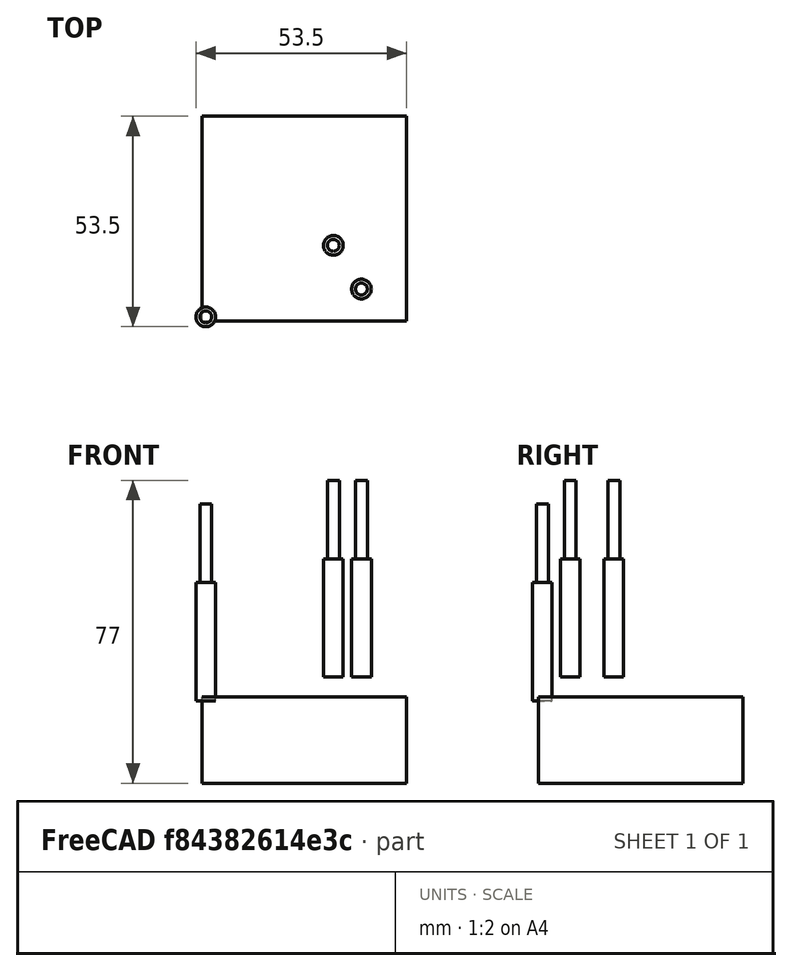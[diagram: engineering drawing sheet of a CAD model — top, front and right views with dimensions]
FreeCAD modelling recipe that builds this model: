
FCSTD DOCUMENT  (FreeCAD 1.0R39109 (Git))
Label: test CNCFCStd
License: All rights reserved
LicenseURL: http://en.wikipedia.org/wiki/All_rights_reserved
objects: Part::FeaturePython×6, Path::FeaturePython×4, Mesh::FeaturePython×4, Sketcher::SketchObject×3, App::DocumentObjectGroup×3, PartDesign::Pocket×2, PartDesign::Pad×1, App::FeaturePython×1, PartDesign::Body×1
note: 23 computed .brp shape members not serialized (recipe doc carries the construction recipe); baked Part::Feature solids carry a one-line shape summary decoded from their .brp

FEATURE [Sketcher::SketchObject] Sketch
  ArcFitTolerance = 1e-06
  AttachmentSupport = -> [XY_Plane]
  FullyConstrained = false
  MakeInternals = false
  MapMode = 5
  sketch-geometry (5):
    g0: LineSegment StartX=-25 StartY=25 StartZ=0 EndX=-25 EndY=-25 EndZ=0
    g1: LineSegment StartX=-25 StartY=-25 StartZ=0 EndX=25 EndY=-25 EndZ=0
    g2: LineSegment StartX=25 StartY=-25 StartZ=0 EndX=25 EndY=25 EndZ=0
    g3: LineSegment StartX=25 StartY=25 StartZ=0 EndX=-25 EndY=25 EndZ=0
    g4: Circle CenterX=-12.7394 CenterY=-12.191 CenterZ=0 NormalX=0 NormalY=0 NormalZ=1 AngleXU=0 Radius=4.56572
  constraints (11):
    c: Coincident(g0,g1)
    c: Coincident(g1,g2)
    c: Coincident(g2,g3)
    c: Coincident(g3,g0)
    c: Vertical(g0)
    c: Vertical(g2)
    c: Horizontal(g1)
    c: Horizontal(g3)
    c: Distance(g3,g3) = 50
    c: Distance(g0,g0) = 50
    c: Symmetric(g0,g1,g-1)
FEATURE [PartDesign::Pad] Pad
  Direction = (0,0,1)
  Length = 20
  Length2 = 0
  Profile = -> Sketch
  ReferenceAxis = -> Sketch [N_Axis]
  Reversed = true
  Suppressed = false
  Type = 0
FEATURE [Sketcher::SketchObject] Sketch001
  ArcFitTolerance = 1e-06
  AttachmentSupport = -> [XY_Plane]
  FullyConstrained = false
  MakeInternals = false
  MapMode = 5
  sketch-geometry (4):
    g0: LineSegment StartX=-18.6884 StartY=17.0009 StartZ=0 EndX=-18.6884 EndY=-0.101786 EndZ=0
    g1: LineSegment StartX=-18.6884 StartY=-0.101786 StartZ=0 EndX=17.0304 EndY=-0.101786 EndZ=0
    g2: LineSegment StartX=17.0304 StartY=-0.101786 StartZ=0 EndX=17.0304 EndY=17.0009 EndZ=0
    g3: LineSegment StartX=17.0304 StartY=17.0009 StartZ=0 EndX=-18.6884 EndY=17.0009 EndZ=0
  constraints (8):
    c: Coincident(g0,g1)
    c: Coincident(g1,g2)
    c: Coincident(g2,g3)
    c: Coincident(g3,g0)
    c: Vertical(g0)
    c: Vertical(g2)
    c: Horizontal(g1)
    c: Horizontal(g3)
FEATURE [PartDesign::Pocket] Pocket
  BaseFeature = -> Pad
  Direction = (0,0,-1)
  Length = 10
  Length2 = 5
  Profile = -> Sketch001
  ReferenceAxis = -> Sketch001 [N_Axis]
  Suppressed = false
  Type = 0
FEATURE [App::FeaturePython] SetupSheet  # Path/CAM operation (typed FeaturePython)
  ClearanceHeightExpression = OpStockZMax+SetupSheet.ClearanceHeightOffset
  ClearanceHeightOffset = 5
  CoolantMode = 0
  CoolantModes = None | Flood | Mist
  FinalDepthExpression = OpFinalDepth
  HorizRapid = 0
  SafeHeightExpression = OpStockZMax+SetupSheet.SafeHeightOffset
  SafeHeightOffset = 3
  StartDepthExpression = OpStartDepth
  StepDownExpression = OpToolDiameter
  VertRapid = 0
FEATURE [Part::FeaturePython] ToolBit  label="Endmill"  # Path/CAM toolbit (typed FeaturePython)
  BitPropertyNames = Chipload | CuttingEdgeHeight | Diameter | Flutes | Length | Material | ShankDiameter | SpindleDirection
  BitShape = <path>
  Chipload = 0
  CuttingEdgeHeight = 30
  Diameter = 5
  Flutes = 0
  Length = 50
  Material = 0
  ShankDiameter = 3
  ShapeName = endmill
  SpindleDirection = 0
FEATURE [Path::FeaturePython] TC__Default_Tool  label="TC: Default Tool"  # Path/CAM operation (typed FeaturePython)
  HorizFeed = 0
  HorizRapid = 0
  SpindleDir = 0
  SpindleSpeed = 0
  Tool = -> ToolBit
  ToolNumber = 1
  VertFeed = 0
  VertRapid = 0
  expr: HorizRapid = SetupSheet.HorizRapid
  expr: VertRapid = SetupSheet.VertRapid
FEATURE [Part::FeaturePython] ToolBit001  label="5mm Endmill"  # Path/CAM toolbit (typed FeaturePython)
  BitPropertyNames = Chipload | CuttingEdgeHeight | Diameter | Flutes | Length | Material | ShankDiameter | SpindleDirection
  BitShape = <path>
  Chipload = 0
  CuttingEdgeHeight = 30
  Diameter = 5
  File = <userpath>/AppData/Roaming/FreeCAD/Macro/Bit/5mm_Endmill.fctb
  Flutes = 0
  Length = 50
  Material = 0
  ShankDiameter = 3
  ShapeName = endmill
  SpindleDirection = 0
FEATURE [Path::FeaturePython] _mm_Endmill  label="5mm Endmill001"  # Path/CAM operation (typed FeaturePython)
  HorizFeed = 2
  HorizRapid = 0
  SpindleDir = 0
  SpindleSpeed = 5000
  Tool = -> ToolBit001
  ToolNumber = 2
  VertFeed = 2
  VertRapid = 0
  expr: HorizRapid = SetupSheet.HorizRapid
  expr: VertRapid = SetupSheet.VertRapid
FEATURE [App::DocumentObjectGroup] Tools
  Group = -> [TC__Default_Tool,_mm_Endmill]
FEATURE [Sketcher::SketchObject] Sketch002
  ArcFitTolerance = 1e-06
  AttachmentSupport = -> [XY_Plane]
  FullyConstrained = false
  MakeInternals = false
  MapMode = 5
  sketch-geometry (4):
    g0: ArcOfCircle CenterX=7.55026 CenterY=-9.04879 CenterZ=0 NormalX=0 NormalY=0 NormalZ=1 AngleXU=0 Radius=4.73311 StartAngle=0.866824 EndAngle=4.00842
    g1: ArcOfCircle CenterX=16.0485 CenterY=-16.2646 CenterZ=0 NormalX=0 NormalY=0 NormalZ=1 AngleXU=0 Radius=4.73311 StartAngle=4.00842 EndAngle=7.15001
    g2: LineSegment StartX=10.6138 StartY=-5.44084 StartZ=0 EndX=19.112 EndY=-12.6567 EndZ=0
    g3: LineSegment StartX=4.48675 StartY=-12.6567 StartZ=0 EndX=12.985 EndY=-19.8726 EndZ=0
  constraints (5):
    c: Tangent(g0,g2) = 1.5708
    c: Tangent(g0,g3) = -1.5708
    c: Tangent(g1,g2) = 1.5708
    c: Tangent(g1,g3) = -1.5708
    c: Equal(g0,g1)
FEATURE [PartDesign::Pocket] Pocket001
  BaseFeature = -> Pocket
  Direction = (0,0,-1)
  Length = 10
  Length2 = 5
  Profile = -> Sketch002
  ReferenceAxis = -> Sketch002 [N_Axis]
  Suppressed = false
  Type = 0
FEATURE [PartDesign::Body] Body
  AllowCompound = false
  Group = -> [Sketch,Pad,Sketch001,Pocket,Sketch002,Pocket001]
  Origin = -> Origin
  Tip = -> Pocket001
FEATURE [Part::FeaturePython] Clone  label="Model-Body"  # Draft clone (typed FeaturePython)
  AttacherType = Attacher::AttachEngine3D
  Fuse = false
  Objects = -> [Body]
  PathResource = Model
  Placement = pos=(25,25,0) rot=(0,0,1;0rad)
  Scale = (1,1,1)
FEATURE [App::DocumentObjectGroup] Model
  Group = -> [Clone]
FEATURE [Part::FeaturePython] Stock001  # WARN: FeaturePython — macro-defined, semantics opaque (R4)
  Base = -> Model
  ExtXneg = 1
  ExtXpos = 1
  ExtYneg = 1
  ExtYpos = 1
  ExtZneg = 1
  ExtZpos = 1
  Placement = pos=(0,0,-20) rot=(0,0,1;0rad)
  StockType = FromBase
FEATURE [Path::FeaturePython] Pocket_Shape  # Path/CAM operation (typed FeaturePython)
  Active = true
  AreaParams:
    Tolerance = 1e-07
    FitArcs = True
    Simplify = False
    CleanDistance = 0.0
    Accuracy = 0.01
    Unit = 1.0
    MinArcPoints = 4
    MaxArcPoints = 100
    ClipperScale = 10000000.0
    Fill = 0
    Coplanar = 0
    Reorient = True
    Outline = False
    Explode = False
    OpenMode = 0
    Deflection = 0.01
    SubjectFill = 0
    ClipFill = 0
    Offset = 0.0
    ExtraPass = 0
    Stepover = 0.0
    LastStepover = 0.0
    JoinType = 0
    EndType = 0
    MiterLimit = 2.0
    RoundPrecision = 0.0
    PocketMode = 2
    ToolRadius = 2.5
    PocketExtraOffset = 0.0
    PocketStepover = 5.0
    PocketLastStepover = 0.0
    FromCenter = True
    Angle = 45.0
    AngleShift = 0.0
    Shift = 0.0
    Thicken = False
    SectionCount = -1
    Stepdown = 1.0
    SectionOffset = 0.0
    SectionTolerance = 1e-06
    SectionMode = 2
    Project = False
  Base = -> [Clone]
  ClearanceHeight = 6
  CoolantMode = 0
  CutMode = 0
  CycleTime = 00:02:08
  ExtensionCorners = true
  ExtensionLengthDefault = 2.5
  ExtraOffset = 0
  FinalDepth = -10
  FinishDepth = 0
  KeepToolDown = false
  MinTravel = false
  OffsetPattern = 1
  OpFinalDepth = -10
  OpStartDepth = 1
  OpStockZMax = 1
  OpStockZMin = -21
  OpToolDiameter = 5
  PathParams = {'orientation': 1, 'feedrate': 2.0, 'feedrate_v': 2.0, 'verbose': True, 'resume_height': 4.0, 'retraction': 6.0, 'return_end': True, 'preamble': False, 'sort_mode': 0}
  PocketLastStepOver = 0
  SafeHeight = 4
  SplitArcs = false
  StartAt = 0
  StartDepth = 1
  StartPoint = (0,0,0)
  StepDown = 5
  StepOver = 100
  ToolController = -> _mm_Endmill
  UseOutline = false
  UseRestMachining = false
  UseStartPoint = false
  ZigZagAngle = 45
  expr: ClearanceHeight = OpStockZMax + SetupSheet.ClearanceHeightOffset
  expr: ExtensionLengthDefault = OpToolDiameter / 2
  expr: FinalDepth = OpFinalDepth
  expr: SafeHeight = OpStockZMax + SetupSheet.SafeHeightOffset
  expr: StartDepth = OpStartDepth
  expr: StepDown = OpToolDiameter
FEATURE [App::DocumentObjectGroup] Operations
  Group = -> [Pocket_Shape]
FEATURE [Path::FeaturePython] Job  # Path/CAM operation (typed FeaturePython)
  CycleTime = 00:02:08
  Fixtures = G54
  GeometryTolerance = 0
  JobType = 0
  Model = -> Model
  Operations = -> Operations
  OrderOutputBy = 0
  PostProcessor = 10
  PostProcessorOutputFile = <path>
  SetupSheet = -> SetupSheet
  SplitOutput = false
  Stock = -> Stock001
  Tools = -> Tools
FEATURE [Part::FeaturePython] CutTool  # WARN: FeaturePython — macro-defined, semantics opaque (R4)
  Placement = pos=(32.4232,18.1727,6) rot=(0,0,1;0rad)
FEATURE [Mesh::FeaturePython] CutMaterial  # WARN: FeaturePython — macro-defined, semantics opaque (R4)
FEATURE [Mesh::FeaturePython] CutMaterialIn  # WARN: FeaturePython — macro-defined, semantics opaque (R4)
FEATURE [Part::FeaturePython] CutTool001  # WARN: FeaturePython — macro-defined, semantics opaque (R4)
  Placement = pos=(39.5432,7.08396,6) rot=(0,0,1;0rad)
FEATURE [Mesh::FeaturePython] CutMaterial001  # WARN: FeaturePython — macro-defined, semantics opaque (R4)
FEATURE [Mesh::FeaturePython] CutMaterialIn001  # WARN: FeaturePython — macro-defined, semantics opaque (R4)
note: 3 file-system paths scrubbed to <path> (originals preserved in the JSON sidecar)
